# Revit family: Sveteco 8
name_source: partatom
category: Осветительные приборы
revit_build: Autodesk Revit 2017 (Build: 20160225_1515(x64)
units: mm (PartAtom-declared; Revit-internal decimal feet)

## family parameters
Источник света = Да
Общий = Нет
Основа = Грань
При загрузке вырезать с полостями = Нет
Размер круглого соединителя = Использовать диаметр
Тип детали = Нормальный
Точка расчета площади = Нет

## types (6) — shared parameters
Видимая форма излучения при визуализации = Нет
Изготовитель = LEDEL
Излучение по диаметру окружности = 152 мм
Комментарии к типоразмеру = Бытовые
Отметка по умолчанию = 1219 мм
Полная установленная мощность = 10 В·А
Светофильтр = 16777215
Смещение цветовой температуры при затухании лампы = <Нет>
Угол наклона = 90.00°

## per-type parameters (varying)
| type | Артикул | Файл фотометрической сетки |
| Sveteco NEW-8-10-Д-5.0K | 502010 | Sveteco NEW-8-10-Д-5.0К-02.ies |
| Sveteco NEW-8-10-Д-4.0K | 202001000842100 | Sveteco NEW-8-10-Д-4.0К-02.ies |
| Sveteco NEW-8-10-Д-4.0К-02 с датчиком звука | 202001000842109
202001000842109 | Sveteco NEW-8-10-Д-4.0К-02 с датчиком звука.ies |
| Sveteco NEW-8-10-Д-5.0К-02 с датчиком звука | 502020 | Sveteco NEW-8-10-Д-5.0К-02.ies |
| Sveteco NEW-8-10-Д-4.0К-02-12-36 DC | 202001000842103 | Sveteco NEW-8-10-Д-4.0К-02-12-36 DC.ies |
| Sveteco NEW-8-10-Д-5.0К-02-12-36 DC | 502016 | Sveteco NEW-8-10-Д-5.0К-02-12-36 DC.ies |

## geometry (parser evidence)
native form markers: Sweep x3
no freeform markers — native parametric forms only
